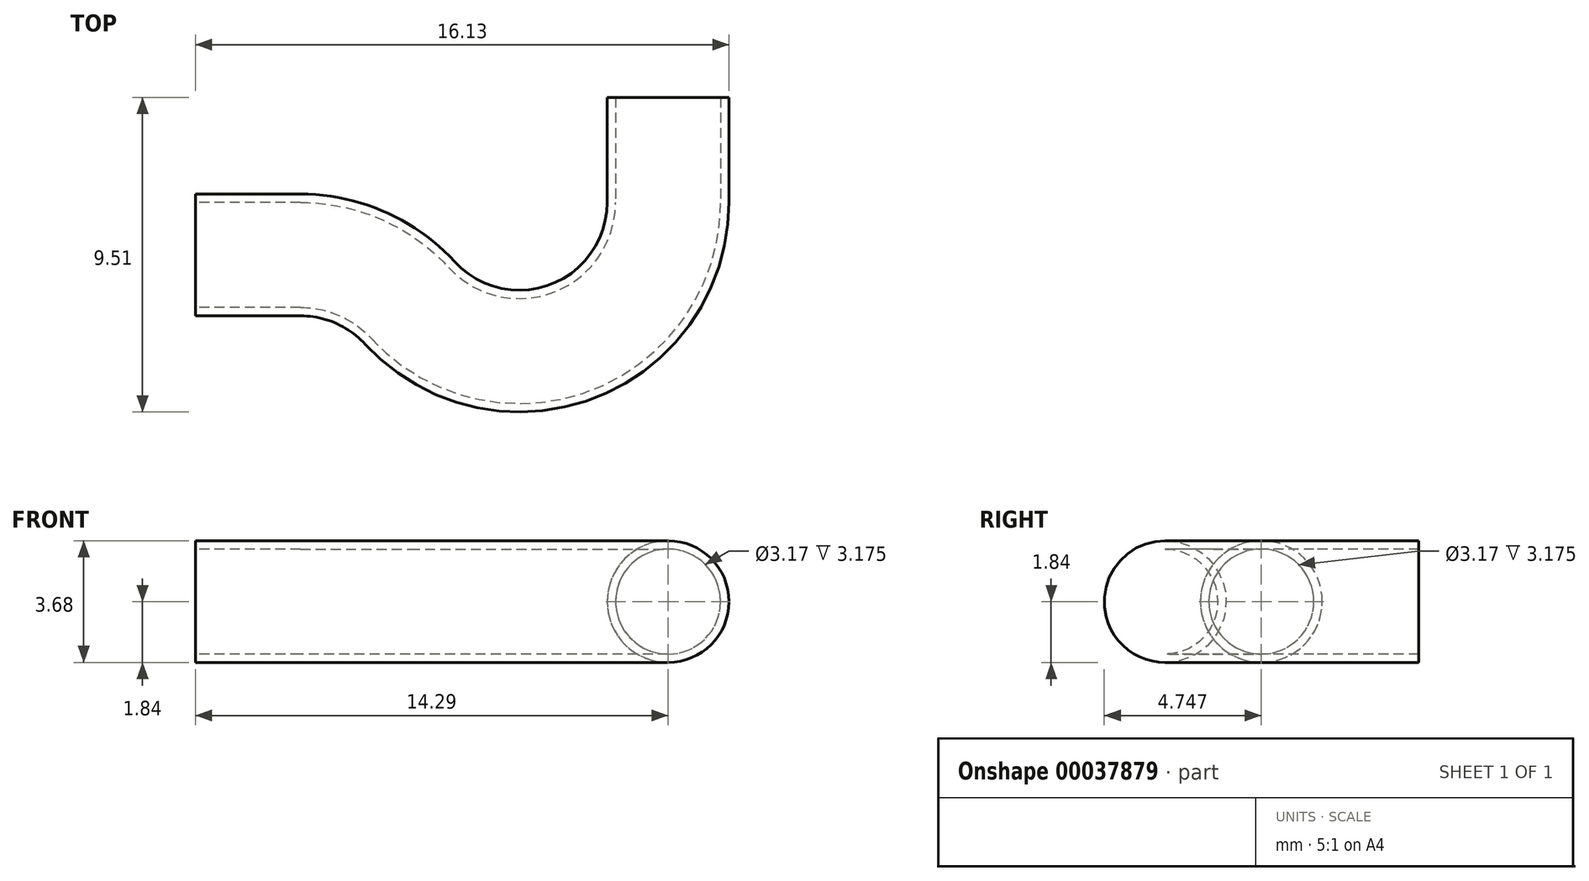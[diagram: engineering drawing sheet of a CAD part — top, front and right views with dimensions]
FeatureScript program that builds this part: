
annotation { "Feature Type Name" : "Feature", "Feature Type Description" : "" }
export const myFeature = defineFeature(function(context is Context, id is Id, definition is map)
    precondition{}
    {
        {
            var Q0;
            Q0=qCreatedBy(makeId("Top.planeOp"),FACE);
            var sketch = newSketch(context, id + "F0", { "sketchPlane" : qUnion([Q0])});
            skLineSegment(sketch, "E0", {"start": v(-15.88, 0) * mm, "end": v(0, 0) * mm, "construction": true});
            skLineSegment(sketch, "E1", {"start": v(-15.88, 0) * mm, "end": v(-15.88, -4.76) * mm, "construction": true});
            skLineSegment(sketch, "E2", {"start": v(-15.88, -4.76) * mm, "end": v(-14.29, -4.76) * mm, "construction": true});
            skLineSegment(sketch, "E3", {"start": v(0, 0) * mm, "end": v(0, -3.18) * mm});
            skLineSegment(sketch, "E4", {"start": v(-14.29, -4.76) * mm, "end": v(-11.11, -4.76) * mm});
            skArc(sketch, "E5", {"start": v(-7.8, -6.22) * mm, "mid": v(-9.3, -5.14) * mm, "end": v(-11.11, -4.76) * mm});
            skArc(sketch, "E6", {"start": v(-7.8, -6.22) * mm, "mid": v(-2.86, -7.36) * mm, "end": v(0, -3.18) * mm});
            skSolve(sketch);
        }
        {
            var Q0;
            Q0=qCreatedBy(makeId("Front.planeOp"),FACE);
            var sketch = newSketch(context, id + "F1", { "sketchPlane" : qUnion([Q0])});
            skLineSegment(sketch, "E7.rect.bottom", {"start": v(1.84, -1.84) * mm, "end": v(-1.84, -1.84) * mm});
            skLineSegment(sketch, "E7.rect.top", {"start": v(1.84, 1.84) * mm, "end": v(-1.84, 1.84) * mm});
            skLineSegment(sketch, "E7.rect.left", {"start": v(1.84, -1.84) * mm, "end": v(1.84, 1.84) * mm});
            skLineSegment(sketch, "E7.rect.right", {"start": v(-1.84, -1.84) * mm, "end": v(-1.84, 1.84) * mm});
            skPoint(sketch, "E7.rect.middle", {"position": v(0, 0) * mm});
            skCircle(sketch, "E8", {"center": v(0, 0) * mm, "radius": 1.59 * mm});
            skSolve(sketch);
        }
        {
            var Q0;
            Q0 = qSketchRegion(id + "F1", true);
            var Q1;
            Q1=sQuery(id+"F0.wireOp",EDGE,"E3");
            var Q2;
            Q2=sQuery(id+"F0.wireOp",EDGE,"E6");
            var Q3;
            Q3=sQuery(id+"F0.wireOp",EDGE,"E5");
            var Q4;
            Q4=sQuery(id+"F0.wireOp",EDGE,"E4");
            sweep(context, id + "F2", {"profiles" : qUnion([Q0]), "path" : qUnion([Q1, Q2, Q3, Q4])});
        }
        {
            var Q0;
            Q0=makeQuery(id+"F2.opSweep","SWEPT_EDGE",EDGE,{"disambiguationData":[OSD([sQuery(id+"F0.wireOp",EDGE,"E4"),sQuery(id+"F1.wireOp",EDGE,"E7.rect.bottom"),sQuery(id+"F1.wireOp",EDGE,"E7.rect.left")])]});
            var Q1;
            Q1=makeQuery(id+"F2.opSweep","SWEPT_EDGE",EDGE,{"disambiguationData":[OSD([sQuery(id+"F0.wireOp",EDGE,"E4"),sQuery(id+"F1.wireOp",EDGE,"E7.rect.top"),sQuery(id+"F1.wireOp",EDGE,"E7.rect.left")])]});
            var Q2;
            Q2=makeQuery(id+"F2.opSweep","SWEPT_EDGE",EDGE,{"disambiguationData":[OSD([sQuery(id+"F0.wireOp",EDGE,"E4"),sQuery(id+"F1.wireOp",EDGE,"E7.rect.top"),sQuery(id+"F1.wireOp",EDGE,"E7.rect.right")])]});
            var Q3;
            Q3=makeQuery(id+"F2.opSweep","SWEPT_EDGE",EDGE,{"disambiguationData":[OSD([sQuery(id+"F0.wireOp",EDGE,"E4"),sQuery(id+"F1.wireOp",EDGE,"E7.rect.bottom"),sQuery(id+"F1.wireOp",EDGE,"E7.rect.right")])]});
            fillet(context, id + "F3", {"entities" : qUnion([Q0, Q1, Q2, Q3]), "radius" : 1.84 * mm, "tangentPropagation" : true, "allowEdgeOverflow" : false});
        }
    });
